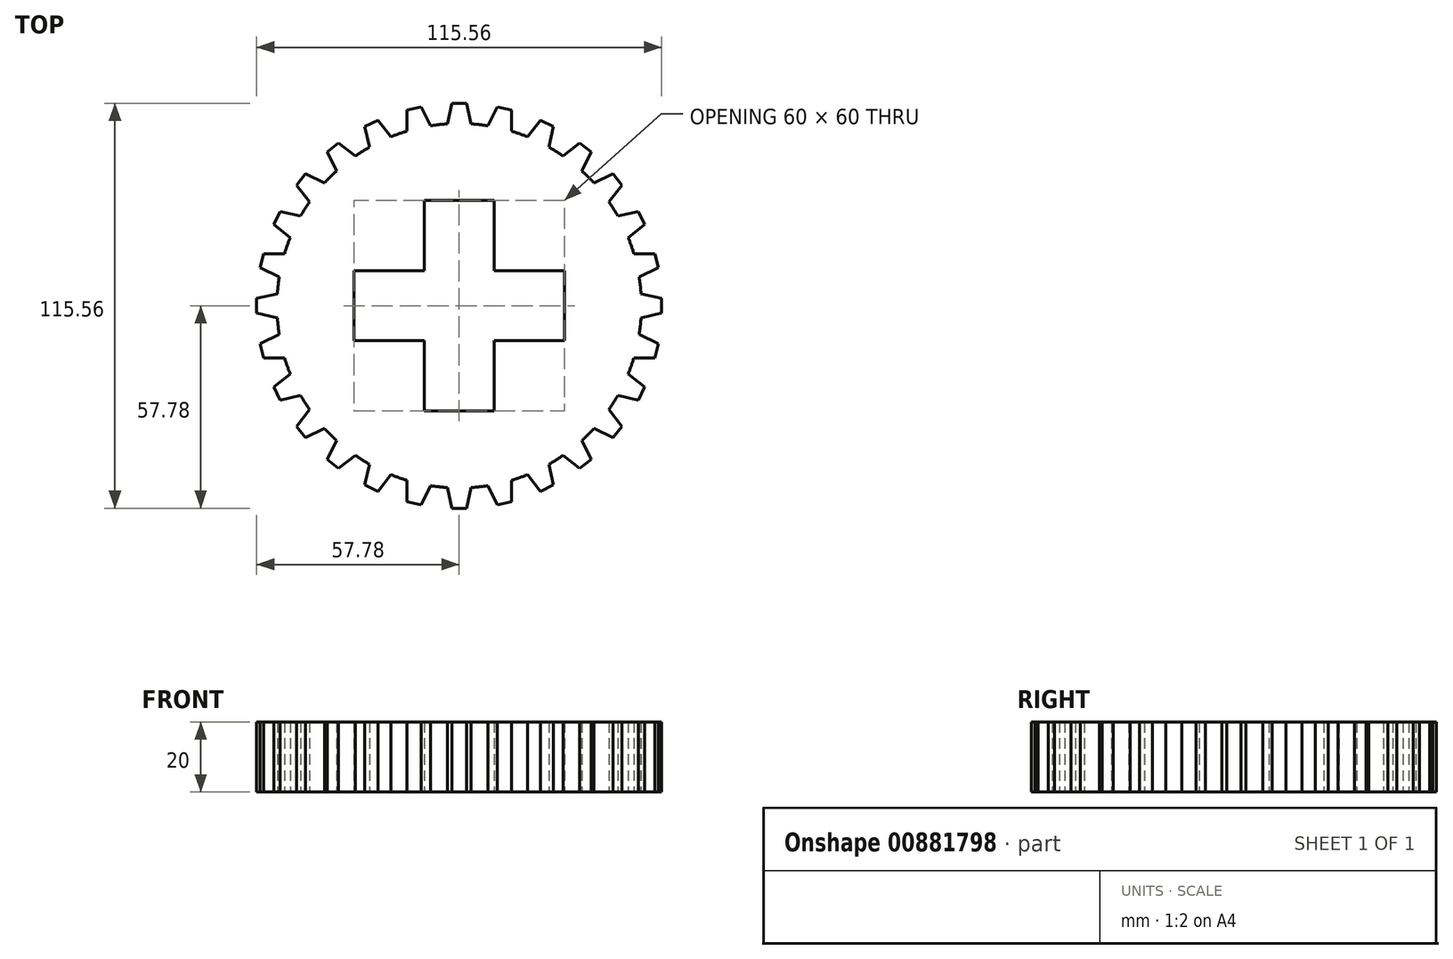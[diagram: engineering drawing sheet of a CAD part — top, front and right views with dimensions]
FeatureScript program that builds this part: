
annotation { "Feature Type Name" : "Feature", "Feature Type Description" : "" }
export const myFeature = defineFeature(function(context is Context, id is Id, definition is map)
    precondition{}
    {
        {
            var Q0;
            Q0=qCreatedBy(makeId("Top.planeOp"),FACE);
            var sketch = newSketch(context, id + "F0", { "sketchPlane" : qUnion([Q0])});
            skCircle(sketch, "E0", {"center": v(0, 0) * mm, "radius": 52 * mm});
            skLineSegment(sketch, "E1", {"start": v(0, 0) * mm, "end": v(0, 30) * mm, "construction": true});
            skLineSegment(sketch, "E2", {"start": v(0, 30) * mm, "end": v(-10, 30) * mm});
            skLineSegment(sketch, "E3", {"start": v(-10, 30) * mm, "end": v(-10, 10) * mm});
            skLineSegment(sketch, "E4", {"start": v(-10, 10) * mm, "end": v(-30, 10) * mm});
            skLineSegment(sketch, "E5", {"start": v(-30, 10) * mm, "end": v(-30, 0) * mm});
            skLineSegment(sketch, "E6.MirrorCS", {"start": v(0, 30) * mm, "end": v(10, 30) * mm});
            skLineSegment(sketch, "E7.MirrorCS", {"start": v(10, 30) * mm, "end": v(10, 10) * mm});
            skLineSegment(sketch, "E8.MirrorCS", {"start": v(10, 10) * mm, "end": v(30, 10) * mm});
            skLineSegment(sketch, "E9.MirrorCS", {"start": v(30, 10) * mm, "end": v(30, 0) * mm});
            skLineSegment(sketch, "E10.MirrorCS", {"start": v(-30, -10) * mm, "end": v(-30, 0) * mm});
            skLineSegment(sketch, "E11.MirrorCS", {"start": v(-10, -10) * mm, "end": v(-30, -10) * mm});
            skLineSegment(sketch, "E12.MirrorCS", {"start": v(-10, -30) * mm, "end": v(-10, -10) * mm});
            skLineSegment(sketch, "E13.MirrorCS", {"start": v(0, -30) * mm, "end": v(-10, -30) * mm});
            skLineSegment(sketch, "E14.MirrorCS", {"start": v(0, -30) * mm, "end": v(10, -30) * mm});
            skLineSegment(sketch, "E15.MirrorCS", {"start": v(10, -30) * mm, "end": v(10, -10) * mm});
            skLineSegment(sketch, "E16.MirrorCS", {"start": v(10, -10) * mm, "end": v(30, -10) * mm});
            skLineSegment(sketch, "E17.MirrorCS", {"start": v(30, -10) * mm, "end": v(30, 0) * mm});
            skLineSegment(sketch, "E18", {"start": v(0, 52) * mm, "end": v(0, 63.9) * mm, "construction": true});
            skLineSegment(sketch, "E19", {"start": v(-3.41, 51.89) * mm, "end": v(-2.06, 57.78) * mm});
            skLineSegment(sketch, "E20", {"start": v(-2.06, 57.78) * mm, "end": v(0, 57.78) * mm});
            skLineSegment(sketch, "E21.MirrorCS", {"start": v(2.06, 57.78) * mm, "end": v(0, 57.78) * mm});
            skLineSegment(sketch, "E22.MirrorCS", {"start": v(3.41, 51.89) * mm, "end": v(2.06, 57.78) * mm});
            skLineSegment(sketch, "E23.1.0", {"start": v(-8.22, 51.35) * mm, "end": v(-10.85, 56.79) * mm});
            skLineSegment(sketch, "E23.1.1", {"start": v(-10.85, 56.79) * mm, "end": v(-12.86, 56.33) * mm});
            skLineSegment(sketch, "E23.1.2", {"start": v(-14.86, 55.87) * mm, "end": v(-12.86, 56.33) * mm});
            skLineSegment(sketch, "E23.1.3", {"start": v(-14.87, 49.83) * mm, "end": v(-14.86, 55.87) * mm});
            skLineSegment(sketch, "E23.2.0", {"start": v(-19.44, 48.23) * mm, "end": v(-23.21, 52.95) * mm});
            skLineSegment(sketch, "E23.2.1", {"start": v(-23.21, 52.95) * mm, "end": v(-25.07, 52.05) * mm});
            skLineSegment(sketch, "E23.2.2", {"start": v(-26.92, 51.16) * mm, "end": v(-25.07, 52.05) * mm});
            skLineSegment(sketch, "E23.2.3", {"start": v(-25.59, 45.27) * mm, "end": v(-26.92, 51.16) * mm});
            skLineSegment(sketch, "E23.3.0", {"start": v(-29.68, 42.7) * mm, "end": v(-34.41, 46.46) * mm});
            skLineSegment(sketch, "E23.3.1", {"start": v(-34.41, 46.46) * mm, "end": v(-36.02, 45.17) * mm});
            skLineSegment(sketch, "E23.3.2", {"start": v(-37.63, 43.89) * mm, "end": v(-36.02, 45.17) * mm});
            skLineSegment(sketch, "E23.3.3", {"start": v(-35.02, 38.44) * mm, "end": v(-37.63, 43.89) * mm});
            skLineSegment(sketch, "E23.4.0", {"start": v(-38.44, 35.02) * mm, "end": v(-43.89, 37.63) * mm});
            skLineSegment(sketch, "E23.4.1", {"start": v(-43.89, 37.63) * mm, "end": v(-45.17, 36.02) * mm});
            skLineSegment(sketch, "E23.4.2", {"start": v(-46.46, 34.41) * mm, "end": v(-45.17, 36.02) * mm});
            skLineSegment(sketch, "E23.4.3", {"start": v(-42.7, 29.68) * mm, "end": v(-46.46, 34.41) * mm});
            skLineSegment(sketch, "E23.5.0", {"start": v(-45.27, 25.59) * mm, "end": v(-51.16, 26.92) * mm});
            skLineSegment(sketch, "E23.5.1", {"start": v(-51.16, 26.92) * mm, "end": v(-52.05, 25.07) * mm});
            skLineSegment(sketch, "E23.5.2", {"start": v(-52.95, 23.21) * mm, "end": v(-52.05, 25.07) * mm});
            skLineSegment(sketch, "E23.5.3", {"start": v(-48.23, 19.44) * mm, "end": v(-52.95, 23.21) * mm});
            skLineSegment(sketch, "E23.6.0", {"start": v(-49.83, 14.87) * mm, "end": v(-55.87, 14.86) * mm});
            skLineSegment(sketch, "E23.6.1", {"start": v(-55.87, 14.86) * mm, "end": v(-56.33, 12.86) * mm});
            skLineSegment(sketch, "E23.6.2", {"start": v(-56.79, 10.85) * mm, "end": v(-56.33, 12.86) * mm});
            skLineSegment(sketch, "E23.6.3", {"start": v(-51.35, 8.22) * mm, "end": v(-56.79, 10.85) * mm});
            skLineSegment(sketch, "E23.7.0", {"start": v(-51.89, 3.41) * mm, "end": v(-57.78, 2.06) * mm});
            skLineSegment(sketch, "E23.7.1", {"start": v(-57.78, 2.06) * mm, "end": v(-57.78, 0) * mm});
            skLineSegment(sketch, "E23.7.2", {"start": v(-57.78, -2.06) * mm, "end": v(-57.78, 0) * mm});
            skLineSegment(sketch, "E23.7.3", {"start": v(-51.89, -3.41) * mm, "end": v(-57.78, -2.06) * mm});
            skLineSegment(sketch, "E23.8.0", {"start": v(-51.35, -8.22) * mm, "end": v(-56.79, -10.85) * mm});
            skLineSegment(sketch, "E23.8.1", {"start": v(-56.79, -10.85) * mm, "end": v(-56.33, -12.86) * mm});
            skLineSegment(sketch, "E23.8.2", {"start": v(-55.87, -14.86) * mm, "end": v(-56.33, -12.86) * mm});
            skLineSegment(sketch, "E23.8.3", {"start": v(-49.83, -14.87) * mm, "end": v(-55.87, -14.86) * mm});
            skLineSegment(sketch, "E23.9.0", {"start": v(-48.23, -19.44) * mm, "end": v(-52.95, -23.21) * mm});
            skLineSegment(sketch, "E23.9.1", {"start": v(-52.95, -23.21) * mm, "end": v(-52.05, -25.07) * mm});
            skLineSegment(sketch, "E23.9.2", {"start": v(-51.16, -26.92) * mm, "end": v(-52.05, -25.07) * mm});
            skLineSegment(sketch, "E23.9.3", {"start": v(-45.27, -25.59) * mm, "end": v(-51.16, -26.92) * mm});
            skLineSegment(sketch, "E23.10.0", {"start": v(-42.7, -29.68) * mm, "end": v(-46.46, -34.41) * mm});
            skLineSegment(sketch, "E23.10.1", {"start": v(-46.46, -34.41) * mm, "end": v(-45.17, -36.02) * mm});
            skLineSegment(sketch, "E23.10.2", {"start": v(-43.89, -37.63) * mm, "end": v(-45.17, -36.02) * mm});
            skLineSegment(sketch, "E23.10.3", {"start": v(-38.44, -35.02) * mm, "end": v(-43.89, -37.63) * mm});
            skLineSegment(sketch, "E23.11.0", {"start": v(-35.02, -38.44) * mm, "end": v(-37.63, -43.89) * mm});
            skLineSegment(sketch, "E23.11.1", {"start": v(-37.63, -43.89) * mm, "end": v(-36.02, -45.17) * mm});
            skLineSegment(sketch, "E23.11.2", {"start": v(-34.41, -46.46) * mm, "end": v(-36.02, -45.17) * mm});
            skLineSegment(sketch, "E23.11.3", {"start": v(-29.68, -42.7) * mm, "end": v(-34.41, -46.46) * mm});
            skLineSegment(sketch, "E23.12.0", {"start": v(-25.59, -45.27) * mm, "end": v(-26.92, -51.16) * mm});
            skLineSegment(sketch, "E23.12.1", {"start": v(-26.92, -51.16) * mm, "end": v(-25.07, -52.05) * mm});
            skLineSegment(sketch, "E23.12.2", {"start": v(-23.21, -52.95) * mm, "end": v(-25.07, -52.05) * mm});
            skLineSegment(sketch, "E23.12.3", {"start": v(-19.44, -48.23) * mm, "end": v(-23.21, -52.95) * mm});
            skLineSegment(sketch, "E23.13.0", {"start": v(-14.87, -49.83) * mm, "end": v(-14.86, -55.87) * mm});
            skLineSegment(sketch, "E23.13.1", {"start": v(-14.86, -55.87) * mm, "end": v(-12.86, -56.33) * mm});
            skLineSegment(sketch, "E23.13.2", {"start": v(-10.85, -56.79) * mm, "end": v(-12.86, -56.33) * mm});
            skLineSegment(sketch, "E23.13.3", {"start": v(-8.22, -51.35) * mm, "end": v(-10.85, -56.79) * mm});
            skLineSegment(sketch, "E23.14.0", {"start": v(-3.41, -51.89) * mm, "end": v(-2.06, -57.78) * mm});
            skLineSegment(sketch, "E23.14.1", {"start": v(-2.06, -57.78) * mm, "end": v(0, -57.78) * mm});
            skLineSegment(sketch, "E23.14.2", {"start": v(2.06, -57.78) * mm, "end": v(0, -57.78) * mm});
            skLineSegment(sketch, "E23.14.3", {"start": v(3.41, -51.89) * mm, "end": v(2.06, -57.78) * mm});
            skLineSegment(sketch, "E23.15.0", {"start": v(8.22, -51.35) * mm, "end": v(10.85, -56.79) * mm});
            skLineSegment(sketch, "E23.15.1", {"start": v(10.85, -56.79) * mm, "end": v(12.86, -56.33) * mm});
            skLineSegment(sketch, "E23.15.2", {"start": v(14.86, -55.87) * mm, "end": v(12.86, -56.33) * mm});
            skLineSegment(sketch, "E23.15.3", {"start": v(14.87, -49.83) * mm, "end": v(14.86, -55.87) * mm});
            skLineSegment(sketch, "E23.16.0", {"start": v(19.44, -48.23) * mm, "end": v(23.21, -52.95) * mm});
            skLineSegment(sketch, "E23.16.1", {"start": v(23.21, -52.95) * mm, "end": v(25.07, -52.05) * mm});
            skLineSegment(sketch, "E23.16.2", {"start": v(26.92, -51.16) * mm, "end": v(25.07, -52.05) * mm});
            skLineSegment(sketch, "E23.16.3", {"start": v(25.59, -45.27) * mm, "end": v(26.92, -51.16) * mm});
            skLineSegment(sketch, "E23.17.0", {"start": v(29.68, -42.7) * mm, "end": v(34.41, -46.46) * mm});
            skLineSegment(sketch, "E23.17.1", {"start": v(34.41, -46.46) * mm, "end": v(36.02, -45.17) * mm});
            skLineSegment(sketch, "E23.17.2", {"start": v(37.63, -43.89) * mm, "end": v(36.02, -45.17) * mm});
            skLineSegment(sketch, "E23.17.3", {"start": v(35.02, -38.44) * mm, "end": v(37.63, -43.89) * mm});
            skLineSegment(sketch, "E23.18.0", {"start": v(38.44, -35.02) * mm, "end": v(43.89, -37.63) * mm});
            skLineSegment(sketch, "E23.18.1", {"start": v(43.89, -37.63) * mm, "end": v(45.17, -36.02) * mm});
            skLineSegment(sketch, "E23.18.2", {"start": v(46.46, -34.41) * mm, "end": v(45.17, -36.02) * mm});
            skLineSegment(sketch, "E23.18.3", {"start": v(42.7, -29.68) * mm, "end": v(46.46, -34.41) * mm});
            skLineSegment(sketch, "E23.19.0", {"start": v(45.27, -25.59) * mm, "end": v(51.16, -26.92) * mm});
            skLineSegment(sketch, "E23.19.1", {"start": v(51.16, -26.92) * mm, "end": v(52.05, -25.07) * mm});
            skLineSegment(sketch, "E23.19.2", {"start": v(52.95, -23.21) * mm, "end": v(52.05, -25.07) * mm});
            skLineSegment(sketch, "E23.19.3", {"start": v(48.23, -19.44) * mm, "end": v(52.95, -23.21) * mm});
            skLineSegment(sketch, "E23.20.0", {"start": v(49.83, -14.87) * mm, "end": v(55.87, -14.86) * mm});
            skLineSegment(sketch, "E23.20.1", {"start": v(55.87, -14.86) * mm, "end": v(56.33, -12.86) * mm});
            skLineSegment(sketch, "E23.20.2", {"start": v(56.79, -10.85) * mm, "end": v(56.33, -12.86) * mm});
            skLineSegment(sketch, "E23.20.3", {"start": v(51.35, -8.22) * mm, "end": v(56.79, -10.85) * mm});
            skLineSegment(sketch, "E23.21.0", {"start": v(51.89, -3.41) * mm, "end": v(57.78, -2.06) * mm});
            skLineSegment(sketch, "E23.21.1", {"start": v(57.78, -2.06) * mm, "end": v(57.78, 0) * mm});
            skLineSegment(sketch, "E23.21.2", {"start": v(57.78, 2.06) * mm, "end": v(57.78, 0) * mm});
            skLineSegment(sketch, "E23.21.3", {"start": v(51.89, 3.41) * mm, "end": v(57.78, 2.06) * mm});
            skLineSegment(sketch, "E23.22.0", {"start": v(51.35, 8.22) * mm, "end": v(56.79, 10.85) * mm});
            skLineSegment(sketch, "E23.22.1", {"start": v(56.79, 10.85) * mm, "end": v(56.33, 12.86) * mm});
            skLineSegment(sketch, "E23.22.2", {"start": v(55.87, 14.86) * mm, "end": v(56.33, 12.86) * mm});
            skLineSegment(sketch, "E23.22.3", {"start": v(49.83, 14.87) * mm, "end": v(55.87, 14.86) * mm});
            skLineSegment(sketch, "E23.23.0", {"start": v(48.23, 19.44) * mm, "end": v(52.95, 23.21) * mm});
            skLineSegment(sketch, "E23.23.1", {"start": v(52.95, 23.21) * mm, "end": v(52.05, 25.07) * mm});
            skLineSegment(sketch, "E23.23.2", {"start": v(51.16, 26.92) * mm, "end": v(52.05, 25.07) * mm});
            skLineSegment(sketch, "E23.23.3", {"start": v(45.27, 25.59) * mm, "end": v(51.16, 26.92) * mm});
            skLineSegment(sketch, "E23.24.0", {"start": v(42.7, 29.68) * mm, "end": v(46.46, 34.41) * mm});
            skLineSegment(sketch, "E23.24.1", {"start": v(46.46, 34.41) * mm, "end": v(45.17, 36.02) * mm});
            skLineSegment(sketch, "E23.24.2", {"start": v(43.89, 37.63) * mm, "end": v(45.17, 36.02) * mm});
            skLineSegment(sketch, "E23.24.3", {"start": v(38.44, 35.02) * mm, "end": v(43.89, 37.63) * mm});
            skLineSegment(sketch, "E23.25.0", {"start": v(35.02, 38.44) * mm, "end": v(37.63, 43.89) * mm});
            skLineSegment(sketch, "E23.25.1", {"start": v(37.63, 43.89) * mm, "end": v(36.02, 45.17) * mm});
            skLineSegment(sketch, "E23.25.2", {"start": v(34.41, 46.46) * mm, "end": v(36.02, 45.17) * mm});
            skLineSegment(sketch, "E23.25.3", {"start": v(29.68, 42.7) * mm, "end": v(34.41, 46.46) * mm});
            skLineSegment(sketch, "E23.26.0", {"start": v(25.59, 45.27) * mm, "end": v(26.92, 51.16) * mm});
            skLineSegment(sketch, "E23.26.1", {"start": v(26.92, 51.16) * mm, "end": v(25.07, 52.05) * mm});
            skLineSegment(sketch, "E23.26.2", {"start": v(23.21, 52.95) * mm, "end": v(25.07, 52.05) * mm});
            skLineSegment(sketch, "E23.26.3", {"start": v(19.44, 48.23) * mm, "end": v(23.21, 52.95) * mm});
            skLineSegment(sketch, "E23.27.0", {"start": v(14.87, 49.83) * mm, "end": v(14.86, 55.87) * mm});
            skLineSegment(sketch, "E23.27.1", {"start": v(14.86, 55.87) * mm, "end": v(12.86, 56.33) * mm});
            skLineSegment(sketch, "E23.27.2", {"start": v(10.85, 56.79) * mm, "end": v(12.86, 56.33) * mm});
            skLineSegment(sketch, "E23.27.3", {"start": v(8.22, 51.35) * mm, "end": v(10.85, 56.79) * mm});
            skSolve(sketch);
        }
        {
            var Q0;
            Q0=qSketchRegion(id+"F0",true);
            extrude(context, id + "F1", {"entities" : qUnion([Q0]), "depth" : 20 * mm, "offsetDistance" : 25 * mm});
        }
    });
